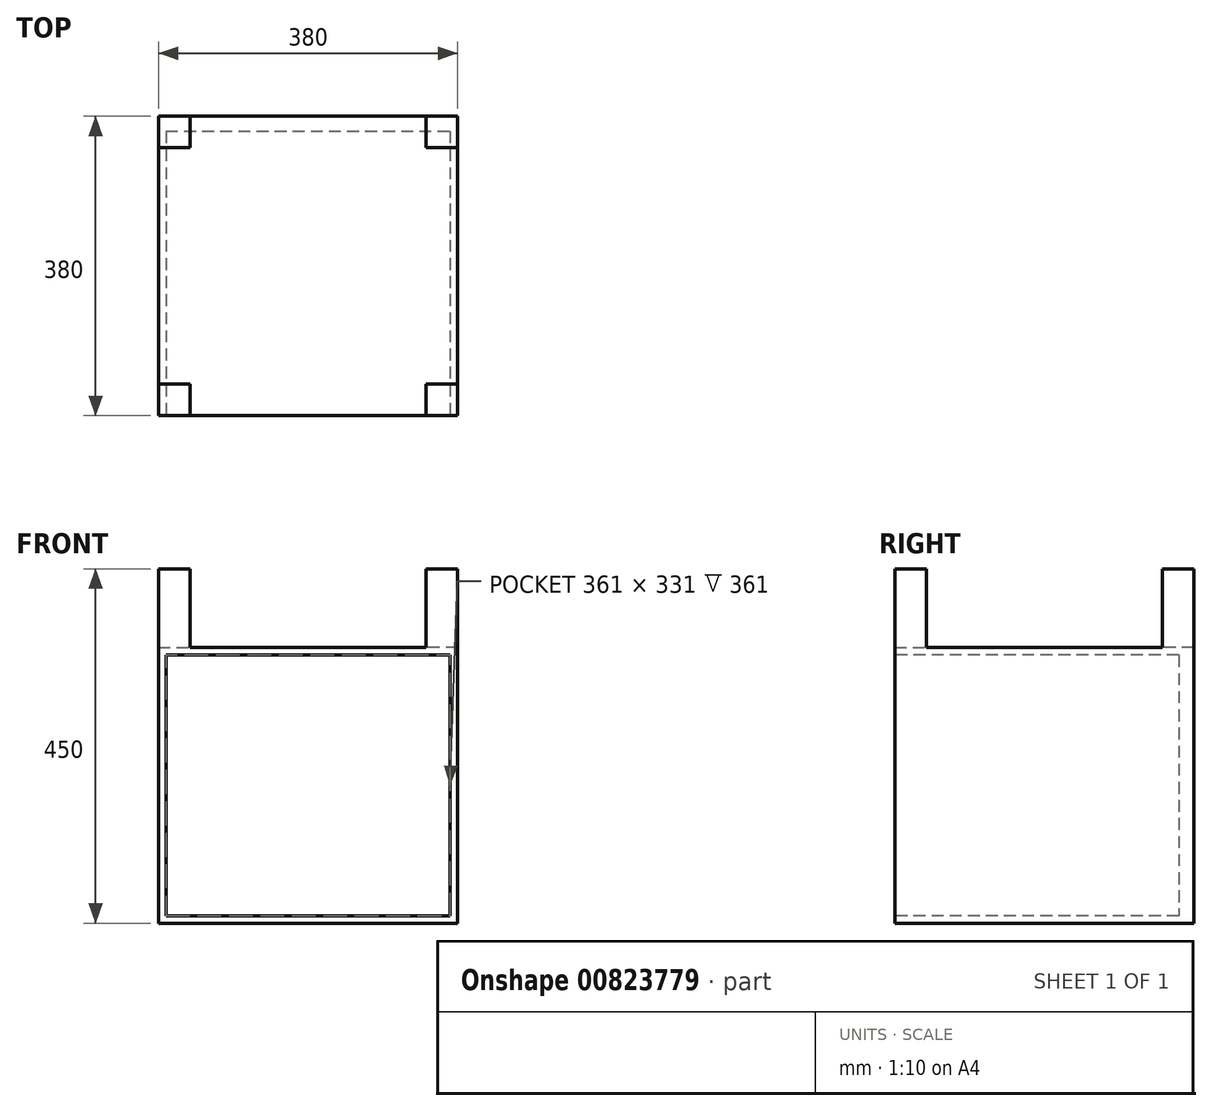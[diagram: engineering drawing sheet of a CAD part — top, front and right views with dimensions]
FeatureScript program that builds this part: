
annotation { "Feature Type Name" : "Feature", "Feature Type Description" : "" }
export const myFeature = defineFeature(function(context is Context, id is Id, definition is map)
    precondition{}
    {
        {
            var Q0;
            Q0=qCreatedBy(makeId("Top.planeOp"),FACE);
            var sketch = newSketch(context, id + "F0", { "sketchPlane" : qUnion([Q0])});
            skLineSegment(sketch, "E0.bottom", {"start": v(190, -190) * mm, "end": v(-190, -190) * mm});
            skLineSegment(sketch, "E0.top", {"start": v(190, 190) * mm, "end": v(-190, 190) * mm});
            skLineSegment(sketch, "E0.left", {"start": v(190, -190) * mm, "end": v(190, 190) * mm});
            skLineSegment(sketch, "E0.right", {"start": v(-190, -190) * mm, "end": v(-190, 190) * mm});
            skPoint(sketch, "E0.middle", {"position": v(0, 0) * mm});
            skSolve(sketch);
        }
        {
            var Q0;
            Q0=makeQuery(id+"F0.imprint","IMPRINT",FACE,{"disambiguationData":[TD([[makeQuery(id+"F0.imprint","IMPRINT",EDGE,{"derivedFrom":sQuery(id+"F0.wireOp",EDGE,"E0.bottom")}),-1.0]])]});
            extrude(context, id + "F1", {"entities" : qUnion([Q0]), "depth" : 350 * mm, "offsetDistance" : 25 * mm});
        }
        {
            var Q0;
            Q0=makeQuery(id+"F1.opExtrude","SWEPT_FACE",FACE,{"disambiguationData":[OSD([sQuery(id+"F0.wireOp",EDGE,"E0.bottom")])]});
            var sketch = newSketch(context, id + "F2", { "sketchPlane" : qUnion([Q0])});
            skLineSegment(sketch, "E1.bottom", {"start": v(-180.5, 340.5) * mm, "end": v(180.5, 340.5) * mm});
            skLineSegment(sketch, "E1.top", {"start": v(-180.5, 9.5) * mm, "end": v(180.5, 9.5) * mm});
            skLineSegment(sketch, "E1.left", {"start": v(-180.5, 340.5) * mm, "end": v(-180.5, 9.5) * mm});
            skLineSegment(sketch, "E1.right", {"start": v(180.5, 340.5) * mm, "end": v(180.5, 9.5) * mm});
            skPoint(sketch, "E1.middle", {"position": v(0, 175) * mm});
            skPoint(sketch, "E1.middle.positionSnap0", {"position": v(190, 175) * mm});
            skPoint(sketch, "E1.centerSnap0", {"position": v(190, 175) * mm});
            skSolve(sketch);
        }
        {
            var Q0;
            Q0=makeQuery(id+"F2.imprint","IMPRINT",FACE,{"disambiguationData":[TD([[makeQuery(id+"F2.imprint","IMPRINT",EDGE,{"derivedFrom":sQuery(id+"F2.wireOp",EDGE,"E1.bottom")}),-1.0]])]});
            extrude(context, id + "F3", {"entities" : qUnion([Q0]), "operationType" : NewBodyOperationType.REMOVE, "oppositeDirection" : true, "depth" : 361 * mm, "offsetDistance" : 25 * mm});
        }
        {
            var Q0;
            Q0=makeQuery(id+"F1.opExtrude","CAP_FACE",FACE,{"disambiguationData":[OSD([sQuery(id+"F0.wireOp",EDGE,"E0.bottom"),sQuery(id+"F0.wireOp",EDGE,"E0.top"),sQuery(id+"F0.wireOp",EDGE,"E0.left"),sQuery(id+"F0.wireOp",EDGE,"E0.right")])],"isStart":false});
            var sketch = newSketch(context, id + "F4", { "sketchPlane" : qUnion([Q0])});
            skLineSegment(sketch, "E2.bottom", {"start": v(-190, 190) * mm, "end": v(-150, 190) * mm});
            skLineSegment(sketch, "E2.top", {"start": v(-190, 150) * mm, "end": v(-150, 150) * mm});
            skLineSegment(sketch, "E2.left", {"start": v(-190, 190) * mm, "end": v(-190, 150) * mm});
            skLineSegment(sketch, "E2.right", {"start": v(-150, 190) * mm, "end": v(-150, 150) * mm});
            skLineSegment(sketch, "E3.bottom", {"start": v(190, 190) * mm, "end": v(150, 190) * mm});
            skLineSegment(sketch, "E3.top", {"start": v(190, 150) * mm, "end": v(150, 150) * mm});
            skLineSegment(sketch, "E3.left", {"start": v(190, 190) * mm, "end": v(190, 150) * mm});
            skLineSegment(sketch, "E3.right", {"start": v(150, 190) * mm, "end": v(150, 150) * mm});
            skLineSegment(sketch, "E4.bottom", {"start": v(190, -190) * mm, "end": v(150, -190) * mm});
            skLineSegment(sketch, "E4.top", {"start": v(190, -150) * mm, "end": v(150, -150) * mm});
            skLineSegment(sketch, "E4.left", {"start": v(190, -190) * mm, "end": v(190, -150) * mm});
            skLineSegment(sketch, "E4.right", {"start": v(150, -190) * mm, "end": v(150, -150) * mm});
            skLineSegment(sketch, "E5.bottom", {"start": v(-190, -190) * mm, "end": v(-150, -190) * mm});
            skLineSegment(sketch, "E5.top", {"start": v(-190, -150) * mm, "end": v(-150, -150) * mm});
            skLineSegment(sketch, "E5.left", {"start": v(-190, -190) * mm, "end": v(-190, -150) * mm});
            skLineSegment(sketch, "E5.right", {"start": v(-150, -190) * mm, "end": v(-150, -150) * mm});
            skSolve(sketch);
        }
        {
            var Q0;
            Q0=makeQuery(id+"F4.imprint","IMPRINT",FACE,{"disambiguationData":[TD([[makeQuery(id+"F4.imprint","IMPRINT",EDGE,{"derivedFrom":sQuery(id+"F4.wireOp",EDGE,"E2.bottom")}),1.0]])]});
            var Q1;
            Q1=makeQuery(id+"F4.imprint","IMPRINT",FACE,{"disambiguationData":[TD([[makeQuery(id+"F4.imprint","IMPRINT",EDGE,{"derivedFrom":sQuery(id+"F4.wireOp",EDGE,"E3.bottom")}),1.0]])]});
            extrude(context, id + "F5", {"entities" : qUnion([Q0, Q1]), "operationType" : NewBodyOperationType.ADD, "depth" : 100 * mm, "offsetDistance" : 25 * mm});
        }
        {
            var Q0;
            Q0=makeQuery(id+"F1.opExtrude","CAP_FACE",FACE,{"disambiguationData":[OSD([sQuery(id+"F0.wireOp",EDGE,"E0.bottom"),sQuery(id+"F0.wireOp",EDGE,"E0.top"),sQuery(id+"F0.wireOp",EDGE,"E0.left"),sQuery(id+"F0.wireOp",EDGE,"E0.right")])],"isStart":false});
            var sketch = newSketch(context, id + "F6", { "sketchPlane" : qUnion([Q0])});
            skLineSegment(sketch, "E6.bottom", {"start": v(-190, -190) * mm, "end": v(-150, -190) * mm});
            skLineSegment(sketch, "E6.top", {"start": v(-190, -150) * mm, "end": v(-150, -150) * mm});
            skLineSegment(sketch, "E6.left", {"start": v(-190, -190) * mm, "end": v(-190, -150) * mm});
            skLineSegment(sketch, "E6.right", {"start": v(-150, -190) * mm, "end": v(-150, -150) * mm});
            skLineSegment(sketch, "E7.bottom", {"start": v(190, -190) * mm, "end": v(150, -190) * mm});
            skLineSegment(sketch, "E7.top", {"start": v(190, -150) * mm, "end": v(150, -150) * mm});
            skLineSegment(sketch, "E7.left", {"start": v(190, -190) * mm, "end": v(190, -150) * mm});
            skLineSegment(sketch, "E7.right", {"start": v(150, -190) * mm, "end": v(150, -150) * mm});
            skSolve(sketch);
        }
        {
            var Q0;
            Q0=makeQuery(id+"F6.imprint","IMPRINT",FACE,{"disambiguationData":[TD([[makeQuery(id+"F6.imprint","IMPRINT",EDGE,{"derivedFrom":sQuery(id+"F6.wireOp",EDGE,"E6.bottom")}),-1.0]])]});
            var Q1;
            Q1=makeQuery(id+"F6.imprint","IMPRINT",FACE,{"disambiguationData":[TD([[makeQuery(id+"F6.imprint","IMPRINT",EDGE,{"derivedFrom":sQuery(id+"F6.wireOp",EDGE,"E7.bottom")}),-1.0]])]});
            extrude(context, id + "F7", {"entities" : qUnion([Q0, Q1]), "operationType" : NewBodyOperationType.ADD, "depth" : 100 * mm, "offsetDistance" : 25 * mm});
        }
    });
